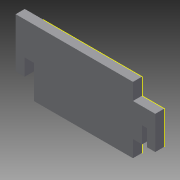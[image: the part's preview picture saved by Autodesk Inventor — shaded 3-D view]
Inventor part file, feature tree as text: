
AUTODESK INVENTOR PART (.ipt)
format: ipt  version: 2015 (Build 190159000, 159)  size: 148,992 bytes
history: native  units: mm
features: sketch x6, extrude x5
ambient origin geometry x8: Origin, YZ Plane, XZ Plane, XY Plane, X Axis, Y Axis, Z Axis, Center Point
bodies: Solid1 (feature_tree)
feature tree (11):
  extrude  "Extrusion1"  Depth=40.0mm
  extrude  "Extrusion2"  TaperAngle=0.0deg  [1 undecoded]
  extrude  "Extrusion3"  Depth=10.0mm
  sketch  "Sketch4"  dims[d6=5.5mm d7=0.0mm]
  extrude  "Extrusion4"  TaperAngle=0.0deg  [1 undecoded]
  extrude  "Extrusion5"  Depth=3.0mm
  sketch  "Sketch1"  dims[d0=60.0mm d1=40.0mm]
  sketch  "Sketch2"  dims[d2=5.5mm d3=0.0mm]
  sketch  "Sketch3"  dims[d4=13.5mm d5=10.0mm]
  sketch  "Sketch5"  dims[d8=5.5mm d9=3.0mm]
  sketch  "Sketch6"  dims[d10=10.0mm d11=5.5mm d12=0.0mm d14=11.0mm d15=10.0mm d16=5.5mm d17=0.0mm d20=0.0mm d21=5.5mm d22=5.5mm d23=0.0mm]
note: 2 required parameter values undecoded (feature->parameter linkage not recoverable at this tier; creation-order binding heuristic only, values carry confidence <= 0.55)
